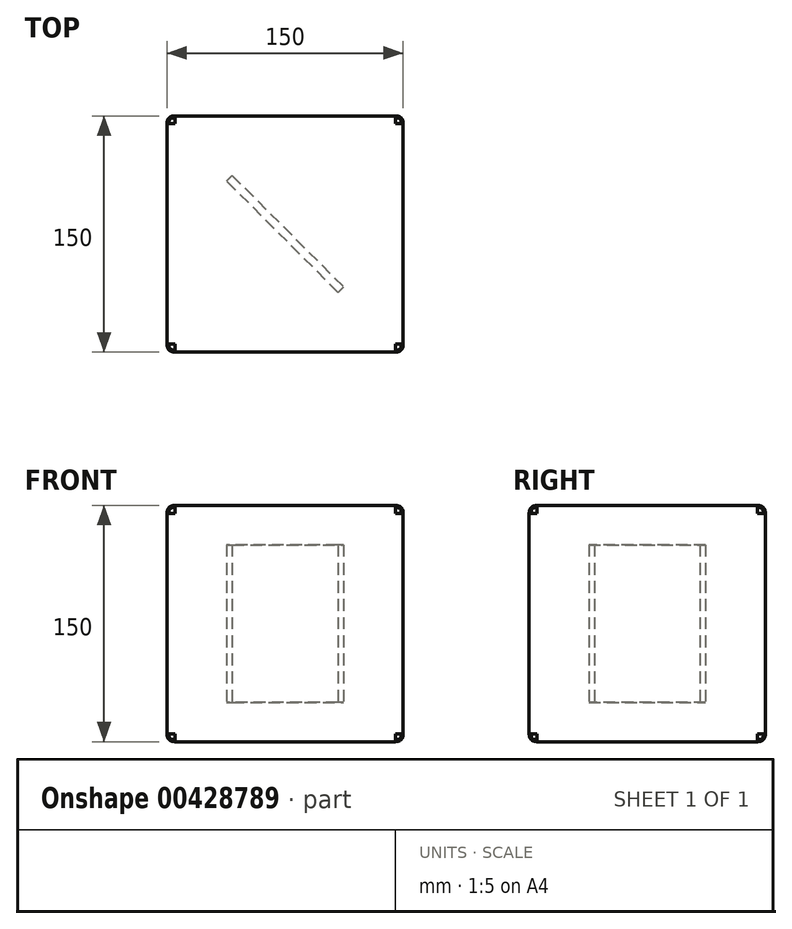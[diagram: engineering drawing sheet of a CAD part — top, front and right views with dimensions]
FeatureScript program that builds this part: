
annotation { "Feature Type Name" : "Feature", "Feature Type Description" : "" }
export const myFeature = defineFeature(function(context is Context, id is Id, definition is map)
    precondition{}
    {
        {
            var Q0;
            Q0=qCreatedBy(makeId("Top.planeOp"),FACE);
            var sketch = newSketch(context, id + "F0", { "sketchPlane" : qUnion([Q0])});
            skLineSegment(sketch, "E0.bottom", {"start": v(75, 75) * mm, "end": v(-75, 75) * mm});
            skLineSegment(sketch, "E0.top", {"start": v(75, -75) * mm, "end": v(-75, -75) * mm});
            skLineSegment(sketch, "E0.left", {"start": v(75, 75) * mm, "end": v(75, -75) * mm});
            skLineSegment(sketch, "E0.right", {"start": v(-75, 75) * mm, "end": v(-75, -75) * mm});
            skPoint(sketch, "E1.middle", {"position": v(0, 0) * mm});
            skSolve(sketch);
        }
        {
            var Q0;
            Q0=qSketchRegion(id+"F0",true);
            extrude(context, id + "F1", {"entities" : qUnion([Q0]), "depth" : 150 * mm});
        }
        {
            var Q0;
            Q0=makeQuery(id+"F1.opExtrude","SWEPT_EDGE",EDGE,{"disambiguationData":[OSD([sQuery(id+"F0.wireOp",EDGE,"E0.top"),sQuery(id+"F0.wireOp",EDGE,"E0.left")])]});
            var Q1;
            Q1=makeQuery(id+"F1.opExtrude","SWEPT_EDGE",EDGE,{"disambiguationData":[OSD([sQuery(id+"F0.wireOp",EDGE,"E0.top"),sQuery(id+"F0.wireOp",EDGE,"E0.right")])]});
            var Q2;
            Q2=makeQuery(id+"F1.opExtrude","SWEPT_EDGE",EDGE,{"disambiguationData":[OSD([sQuery(id+"F0.wireOp",EDGE,"E0.bottom"),sQuery(id+"F0.wireOp",EDGE,"E0.right")])]});
            var Q3;
            Q3=makeQuery(id+"F1.opExtrude","SWEPT_EDGE",EDGE,{"disambiguationData":[OSD([sQuery(id+"F0.wireOp",EDGE,"E0.bottom"),sQuery(id+"F0.wireOp",EDGE,"E0.left")])]});
            var Q4;
            Q4=makeQuery(id+"F1.opExtrude","CAP_EDGE",EDGE,{"disambiguationData":[OSD([sQuery(id+"F0.wireOp",EDGE,"E0.right")])],"isStart":false});
            var Q5;
            Q5=makeQuery(id+"F1.opExtrude","CAP_EDGE",EDGE,{"disambiguationData":[OSD([sQuery(id+"F0.wireOp",EDGE,"E0.bottom")])],"isStart":false});
            var Q6;
            Q6=makeQuery(id+"F1.opExtrude","CAP_EDGE",EDGE,{"disambiguationData":[OSD([sQuery(id+"F0.wireOp",EDGE,"E0.left")])],"isStart":false});
            var Q7;
            Q7=makeQuery(id+"F1.opExtrude","CAP_EDGE",EDGE,{"disambiguationData":[OSD([sQuery(id+"F0.wireOp",EDGE,"E0.top")])],"isStart":false});
            var Q8;
            Q8=makeQuery(id+"F1.opExtrude","CAP_EDGE",EDGE,{"disambiguationData":[OSD([sQuery(id+"F0.wireOp",EDGE,"E0.top")])],"isStart":true});
            var Q9;
            Q9=makeQuery(id+"F1.opExtrude","CAP_EDGE",EDGE,{"disambiguationData":[OSD([sQuery(id+"F0.wireOp",EDGE,"E0.left")])],"isStart":true});
            var Q10;
            Q10=makeQuery(id+"F1.opExtrude","CAP_EDGE",EDGE,{"disambiguationData":[OSD([sQuery(id+"F0.wireOp",EDGE,"E0.right")])],"isStart":true});
            var Q11;
            Q11=makeQuery(id+"F1.opExtrude","CAP_EDGE",EDGE,{"disambiguationData":[OSD([sQuery(id+"F0.wireOp",EDGE,"E0.bottom")])],"isStart":true});
            fillet(context, id + "F2", {"entities" : qUnion([Q0, Q1, Q2, Q3, Q4, Q5, Q6, Q7, Q8, Q9, Q10, Q11]), "radius" : 5 * mm, "tangentPropagation" : true, "rho" : 0.5, "crossSection" : FilletCrossSection.CONIC, "allowEdgeOverflow" : false});
        }
        {
            var Q0;
            Q0=makeQuery(id+"F1.opExtrude","CAP_FACE",FACE,{"disambiguationData":[OSD([sQuery(id+"F0.wireOp",EDGE,"E0.bottom"),sQuery(id+"F0.wireOp",EDGE,"E0.top"),sQuery(id+"F0.wireOp",EDGE,"E0.left"),sQuery(id+"F0.wireOp",EDGE,"E0.right")])],"isStart":true});
            var sketch = newSketch(context, id + "F3", { "sketchPlane" : qUnion([Q0])});
            skLineSegment(sketch, "E2", {"start": v(-37.12, -33.59) * mm, "end": v(-33.59, -37.12) * mm});
            skLineSegment(sketch, "E3", {"start": v(-33.59, -37.12) * mm, "end": v(37.12, 33.59) * mm});
            skLineSegment(sketch, "E4", {"start": v(37.12, 33.59) * mm, "end": v(33.59, 37.12) * mm});
            skLineSegment(sketch, "E5", {"start": v(33.59, 37.12) * mm, "end": v(-37.12, -33.59) * mm});
            skLineSegment(sketch, "E6", {"start": v(35.36, 35.36) * mm, "end": v(-35.36, -35.36) * mm, "construction": true});
            skLineSegment(sketch, "E7", {"start": v(-1.77, 1.77) * mm, "end": v(1.77, -1.77) * mm, "construction": true});
            skLineSegment(sketch, "E8", {"start": v(-75, -75) * mm, "end": v(75, 75) * mm, "construction": true});
            skLineSegment(sketch, "E9", {"start": v(-75, 75) * mm, "end": v(75, -75) * mm, "construction": true});
            skSolve(sketch);
        }
        {
            var Q0;
            Q0 = qSketchRegion(id + "F3", true);
            extrude(context, id + "F4", {"entities" : qUnion([Q0]), "oppositeDirection" : true, "depth" : 125 * mm, "hasSecondDirection" : true, "secondDirectionOppositeDirection" : true, "secondDirectionDepth" : 25 * mm});
        }
    });
